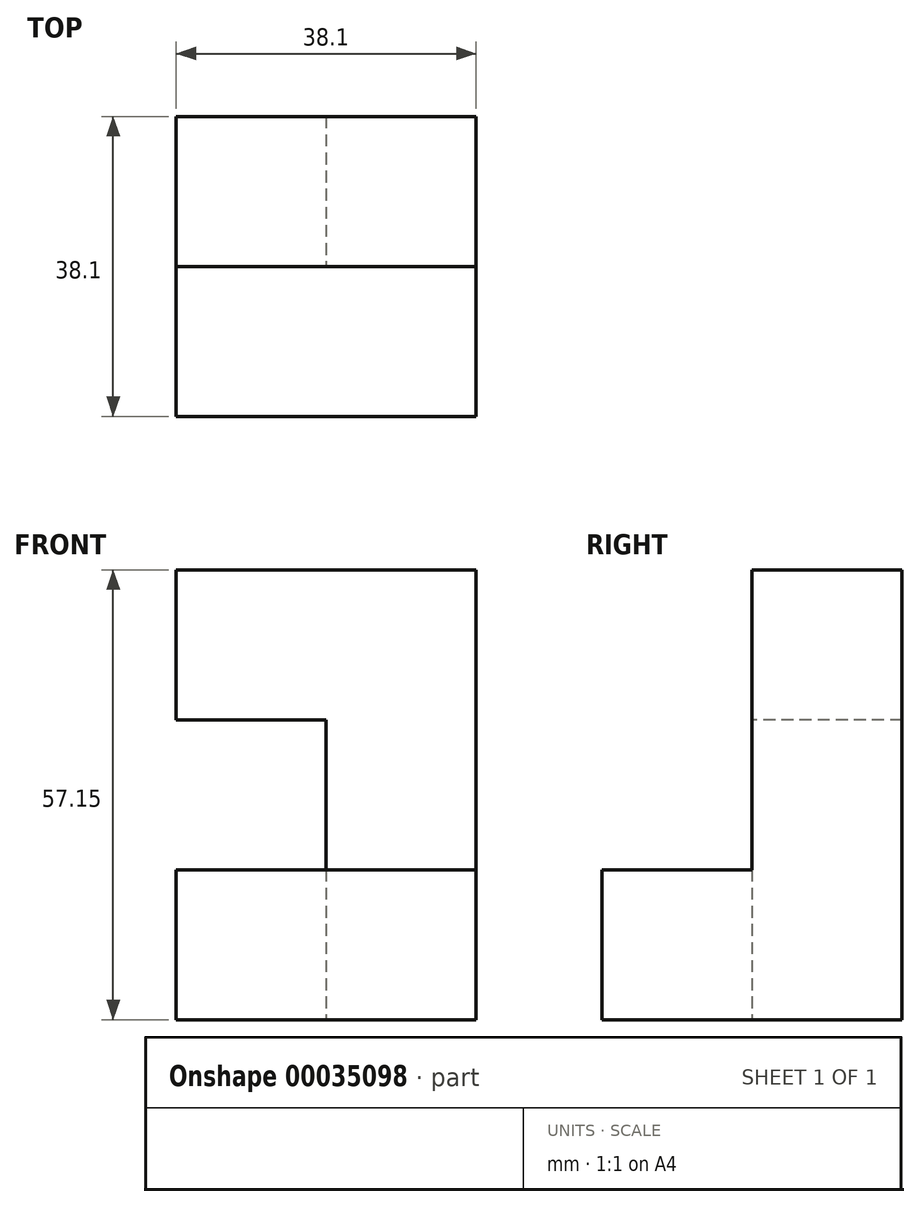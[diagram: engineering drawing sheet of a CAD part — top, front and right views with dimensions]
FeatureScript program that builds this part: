
annotation { "Feature Type Name" : "Feature", "Feature Type Description" : "" }
export const myFeature = defineFeature(function(context is Context, id is Id, definition is map)
    precondition{}
    {
        {
            var Q0;
            Q0=qCreatedBy(makeId("Top.planeOp"),FACE);
            var sketch = newSketch(context, id + "F0", { "sketchPlane" : qUnion([Q0])});
            skLineSegment(sketch, "E0.bottom", {"start": v(0, 0) * mm, "end": v(19.05, 0) * mm});
            skLineSegment(sketch, "E0.top", {"start": v(0, 19.05) * mm, "end": v(19.05, 19.05) * mm});
            skLineSegment(sketch, "E0.left", {"start": v(0, 0) * mm, "end": v(0, 19.05) * mm});
            skLineSegment(sketch, "E0.right", {"start": v(19.05, 0) * mm, "end": v(19.05, 19.05) * mm});
            skSolve(sketch);
        }
        {
            var Q0;
            Q0=makeQuery(id+"F0.imprint","IMPRINT",FACE,{"disambiguationData":[TD([[makeQuery(id+"F0.imprint","IMPRINT",EDGE,{"derivedFrom":sQuery(id+"F0.wireOp",EDGE,"E0.bottom")}),1.0]])]});
            extrude(context, id + "F1", {"entities" : qUnion([Q0]), "depth" : 19.05 * mm});
        }
        {
            var Q0;
            Q0=makeQuery(id+"F1.opExtrude","SWEPT_FACE",FACE,{"disambiguationData":[OSD([sQuery(id+"F0.wireOp",EDGE,"E0.left")])]});
            extrude(context, id + "F2", {"entities" : qUnion([Q0]), "operationType" : NewBodyOperationType.ADD, "depth" : 19.05 * mm});
        }
        {
            var Q0;
            {var subQ0=sQuery(id+"F0.wireOp",EDGE,"E0.top");Q0=makeQuery(id+"F2.boolean.opBoolean","MERGE",FACE,{"derivedFrom":[makeQuery(id+"F1.opExtrude","SWEPT_FACE",FACE,{"disambiguationData":[OSD([subQ0])]}),makeQuery(id+"F2.opExtrude","SWEPT_FACE",FACE,{"disambiguationData":[OSD([subQ0,sQuery(id+"F0.wireOp",EDGE,"E0.left")])]})]});}
            var sketch = newSketch(context, id + "F3", { "sketchPlane" : qUnion([Q0])});
            skLineSegment(sketch, "E1.bottom", {"start": v(-19.05, 19.05) * mm, "end": v(0, 19.05) * mm});
            skLineSegment(sketch, "E1.top", {"start": v(-19.05, 0) * mm, "end": v(0, 0) * mm});
            skLineSegment(sketch, "E1.left", {"start": v(-19.05, 19.05) * mm, "end": v(-19.05, 0) * mm});
            skLineSegment(sketch, "E1.right", {"start": v(0, 19.05) * mm, "end": v(0, 0) * mm});
            skSolve(sketch);
        }
        {
            var Q0;
            Q0=makeQuery(id+"F3.imprint","IMPRINT",FACE,{"disambiguationData":[TD([[makeQuery(id+"F3.imprint","IMPRINT",EDGE,{"derivedFrom":sQuery(id+"F3.wireOp",EDGE,"E1.bottom")}),1.0]])]});
            extrude(context, id + "F4", {"entities" : qUnion([Q0]), "operationType" : NewBodyOperationType.ADD, "depth" : 19.05 * mm});
        }
        {
            var Q0;
            {var subQ0=sQuery(id+"F0.wireOp",EDGE,"E0.left");Q0=makeQuery(id+"F4.boolean.opBoolean","MERGE",FACE,{"derivedFrom":[makeQuery(id+"F2.boolean.opBoolean","MERGE",FACE,{"derivedFrom":[makeQuery(id+"F1.opExtrude","CAP_FACE",FACE,{"disambiguationData":[OSD([sQuery(id+"F0.wireOp",EDGE,"E0.bottom"),sQuery(id+"F0.wireOp",EDGE,"E0.top"),subQ0,sQuery(id+"F0.wireOp",EDGE,"E0.right")])],"isStart":false}),makeQuery(id+"F2.opExtrude","SWEPT_FACE",FACE,{"disambiguationData":[OSD([subQ0]),TDD([makeQuery(id+"F1.opExtrude","CAP_EDGE",EDGE,{"disambiguationData":[OSD([subQ0])],"isStart":false})])]})]}),makeQuery(id+"F4.opExtrude","SWEPT_FACE",FACE,{"disambiguationData":[OSD([sQuery(id+"F3.wireOp",EDGE,"E1.bottom")])]})]});}
            var sketch = newSketch(context, id + "F5", { "sketchPlane" : qUnion([Q0])});
            skLineSegment(sketch, "E2.bottom", {"start": v(0, 38.1) * mm, "end": v(19.05, 38.1) * mm});
            skLineSegment(sketch, "E2.top", {"start": v(0, 19.05) * mm, "end": v(19.05, 19.05) * mm});
            skLineSegment(sketch, "E2.left", {"start": v(0, 38.1) * mm, "end": v(0, 19.05) * mm});
            skLineSegment(sketch, "E2.right", {"start": v(19.05, 38.1) * mm, "end": v(19.05, 19.05) * mm});
            skSolve(sketch);
        }
        {
            var Q0;
            Q0=makeQuery(id+"F5.imprint","IMPRINT",FACE,{"disambiguationData":[TD([[makeQuery(id+"F5.imprint","IMPRINT",EDGE,{"derivedFrom":sQuery(id+"F5.wireOp",EDGE,"E2.bottom")}),-1.0]])]});
            extrude(context, id + "F6", {"entities" : qUnion([Q0]), "operationType" : NewBodyOperationType.ADD, "depth" : 19.05 * mm});
        }
        {
            var Q0;
            Q0=makeQuery(id+"F6.opExtrude","CAP_FACE",FACE,{"disambiguationData":[OSD([sQuery(id+"F5.wireOp",EDGE,"E2.bottom"),sQuery(id+"F5.wireOp",EDGE,"E2.top"),sQuery(id+"F5.wireOp",EDGE,"E2.left"),sQuery(id+"F5.wireOp",EDGE,"E2.right")])],"isStart":false});
            extrude(context, id + "F7", {"entities" : qUnion([Q0]), "operationType" : NewBodyOperationType.ADD, "depth" : 19.05 * mm});
        }
        {
            var Q0;
            {var subQ0=sQuery(id+"F5.wireOp",EDGE,"E2.left");Q0=makeQuery(id+"F7.boolean.opBoolean","MERGE",FACE,{"derivedFrom":[makeQuery(id+"F6.boolean.opBoolean","MERGE",FACE,{"derivedFrom":[makeQuery(id+"F4.opExtrude","SWEPT_FACE",FACE,{"disambiguationData":[OSD([sQuery(id+"F3.wireOp",EDGE,"E1.right")])]}),makeQuery(id+"F6.opExtrude","SWEPT_FACE",FACE,{"disambiguationData":[OSD([subQ0])]})]}),makeQuery(id+"F7.opExtrude","SWEPT_FACE",FACE,{"disambiguationData":[OSD([subQ0])]})]});}
            var sketch = newSketch(context, id + "F8", { "sketchPlane" : qUnion([Q0])});
            skLineSegment(sketch, "E3.bottom", {"start": v(-38.1, 57.15) * mm, "end": v(-19.05, 57.15) * mm});
            skLineSegment(sketch, "E3.top", {"start": v(-38.1, 38.1) * mm, "end": v(-19.05, 38.1) * mm});
            skLineSegment(sketch, "E3.left", {"start": v(-38.1, 57.15) * mm, "end": v(-38.1, 38.1) * mm});
            skLineSegment(sketch, "E3.right", {"start": v(-19.05, 57.15) * mm, "end": v(-19.05, 38.1) * mm});
            skSolve(sketch);
        }
        {
            var Q0;
            Q0=makeQuery(id+"F8.imprint","IMPRINT",FACE,{"disambiguationData":[TD([[makeQuery(id+"F8.imprint","IMPRINT",EDGE,{"derivedFrom":sQuery(id+"F8.wireOp",EDGE,"E3.bottom")}),-1.0]])]});
            extrude(context, id + "F9", {"entities" : qUnion([Q0]), "operationType" : NewBodyOperationType.ADD, "depth" : 19.05 * mm});
        }
    });
